# Revit family: Door-Exterior_Interior-Simpson-French-Full_Arch_Glass-Single
name_source: partatom
category: Doors
revit_build: Autodesk Revit Architecture 2012 (Build: 20110916_2132(x64)
units: mm (PartAtom-declared; Revit-internal decimal feet)

## types (273) — shared parameters
Arch Bottom Height = 0' - 7 19/32"
Assembly Code = B2030230
Bottom Rail Height = 0' - 8 13/16"
Construction Type = Wood
Frame = Wood - Simpson Doors - Douglas Fir
Frame Projection Ext. = 0' - 1"
Frame Projection Int. = 0' - 1"
Frame Type = Frame : Standard
Frame Width = 0' - 3"
Function = Exterior
Glass = Glass - Simpson Doors - Clear
Glass Options = http://simpsondoor.com
Manufacturer = Simpsons Door Company
Middle Rail Height = 0' - 6 3/4"
Muntin Width = 0' - 0 1/2"
Ovolo Construction = Yes
Panel = Wood - Simpson Doors - Douglas Fir
Panel Stile Width = 0' - 4 1/8"
Product Documentation Link = http://www.simpsondoor.com
Product Page URL = http://www.simpsondoor.com
Thickness = 0' - 1 3/4"
Thickness Note = comes in 1 3/4" and 2 1/4" Thickness. Default is set to 1 3/4"
Top Rail Height = 0' - 4 1/32"
URL = http://www.simpsondoor.com
UltraBlock Note = This Door Comes with The Option of UltraBlock Technology. It is Turn On as a Default
UltraBlock Option = Yes
Wall Closure = By host
WaterBarrier Note = This Door Comes with The Option of WaterBarrier with UltraBlock Technology. It is Turn Off as a Default
WaterBarrier with UltraBlock Technology = No
Wood Species = http://simpsondoor.com
Wood Species Note = Available in Any Wood Species

## per-type parameters (varying)
| type | Description | Height | Model | Number of Horizontal Muntins | Number of Vertical Muntins | Rough Height | Rough Width | Width |
| 1401 Exterior French 30x80 Ovolo Flat Panel | Exterior French - Single Lite | 6' - 8" | 1401 | 0 | 0 | 6' - 10" | 2' - 10" | 2' - 6" |
| 1401 Exterior French 30x84 Ovolo Flat Panel | Exterior French - Single Lite | 7' - 0" | 1401 | 0 | 0 | 7' - 2" | 2' - 10" | 2' - 6" |
| 1401 Exterior French 30x96 Ovolo Flat Panel | Exterior French - Single Lite | 8' - 0" | 1401 | 0 | 0 | 8' - 2" | 2' - 10" | 2' - 6" |
| 1401 Exterior French 32x80 Ovolo Flat Panel | Exterior French - Single Lite | 6' - 8" | 1401 | 0 | 0 | 6' - 10" | 3' - 0" | 2' - 8" |
| 1401 Exterior French 32x84 Ovolo Flat Panel | Exterior French - Single Lite | 7' - 0" | 1401 | 0 | 0 | 7' - 2" | 3' - 0" | 2' - 8" |
| 1401 Exterior French 32x96 Ovolo Flat Panel | Exterior French - Single Lite | 8' - 0" | 1401 | 0 | 0 | 8' - 2" | 3' - 0" | 2' - 8" |
| 1401 Exterior French 34x80 Ovolo Flat Panel | Exterior French - Single Lite | 6' - 8" | 1401 | 0 | 0 | 6' - 10" | 3' - 2" | 2' - 10" |
| 1401 Exterior French 34x84 Ovolo Flat Panel | Exterior French - Single Lite | 7' - 0" | 1401 | 0 | 0 | 7' - 2" | 3' - 2" | 2' - 10" |
| 1401 Exterior French 34x96 Ovolo Flat Panel | Exterior French - Single Lite | 8' - 0" | 1401 | 0 | 0 | 8' - 2" | 3' - 2" | 2' - 10" |
| 1401 Exterior French 36x80 Ovolo Flat Panel | Exterior French - Single Lite | 6' - 8" | 1401 | 0 | 0 | 6' - 10" | 3' - 4" | 3' - 0" |
| 1401 Exterior French 36x84 Ovolo Flat Panel | Exterior French - Single Lite | 7' - 0" | 1401 | 0 | 0 | 7' - 2" | 3' - 4" | 3' - 0" |
| 1401 Exterior French 36x96 Ovolo Flat Panel | Exterior French - Single Lite | 8' - 0" | 1401 | 0 | 0 | 8' - 2" | 3' - 4" | 3' - 0" |
| 1401 Exterior French 38x80 Ovolo Flat Panel | Exterior French - Single Lite | 6' - 8" | 1401 | 0 | 0 | 6' - 10" | 3' - 6" | 3' - 2" |
| 1401 Exterior French 38x84 Ovolo Flat Panel | Exterior French - Single Lite | 7' - 0" | 1401 | 0 | 0 | 7' - 2" | 3' - 6" | 3' - 2" |
| 1401 Exterior French 38x96 Ovolo Flat Panel | Exterior French - Single Lite | 8' - 0" | 1401 | 0 | 0 | 8' - 2" | 3' - 6" | 3' - 2" |
| 1401 Exterior French 40x80 Ovolo Flat Panel | Exterior French - Single Lite | 6' - 8" | 1401 | 0 | 0 | 6' - 10" | 3' - 8" | 3' - 4" |
| 1401 Exterior French 40x84 Ovolo Flat Panel | Exterior French - Single Lite | 7' - 0" | 1401 | 0 | 0 | 7' - 2" | 3' - 8" | 3' - 4" |
| 1401 Exterior French 40x96 Ovolo Flat Panel | Exterior French - Single Lite | 8' - 0" | 1401 | 0 | 0 | 8' - 2" | 3' - 8" | 3' - 4" |
| 1401 Exterior French 42x80 Ovolo Flat Panel | Exterior French - Single Lite | 6' - 8" | 1401 | 0 | 0 | 6' - 10" | 3' - 10" | 3' - 6" |
| 1401 Exterior French 42x84 Ovolo Flat Panel | Exterior French - Single Lite | 7' - 0" | 1401 | 0 | 0 | 7' - 2" | 3' - 10" | 3' - 6" |
| 1401 Exterior French 42x96 Ovolo Flat Panel | Exterior French - Single Lite | 8' - 0" | 1401 | 0 | 0 | 8' - 2" | 3' - 10" | 3' - 6" |
| 1410 Exterior French 30x80 Ovolo Flat Panel | Exterior French - Ten Lite | 6' - 8" | 1410 | 4 | 1 | 6' - 10" | 2' - 10" | 2' - 6" |
| 1410 Exterior French 30x84 Ovolo Flat Panel | Exterior French - Ten Lite | 7' - 0" | 1410 | 4 | 1 | 7' - 2" | 2' - 10" | 2' - 6" |
| 1410 Exterior French 30x96 Ovolo Flat Panel | Exterior French - Ten Lite | 8' - 0" | 1410 | 4 | 1 | 8' - 2" | 2' - 10" | 2' - 6" |
| 1410 Exterior French 32x80 Ovolo Flat Panel | Exterior French - Ten Lite | 6' - 8" | 1410 | 4 | 1 | 6' - 10" | 3' - 0" | 2' - 8" |
| 1410 Exterior French 32x84 Ovolo Flat Panel | Exterior French - Ten Lite | 7' - 0" | 1410 | 4 | 1 | 7' - 2" | 3' - 0" | 2' - 8" |
| 1410 Exterior French 32x96 Ovolo Flat Panel | Exterior French - Ten Lite | 8' - 0" | 1410 | 4 | 1 | 8' - 2" | 3' - 0" | 2' - 8" |
| 1410 Exterior French 34x80 Ovolo Flat Panel | Exterior French - Ten Lite | 6' - 8" | 1410 | 4 | 1 | 6' - 10" | 3' - 2" | 2' - 10" |
| 1410 Exterior French 34x84 Ovolo Flat Panel | Exterior French - Ten Lite | 7' - 0" | 1410 | 4 | 1 | 7' - 2" | 3' - 2" | 2' - 10" |
| 1410 Exterior French 34x96 Ovolo Flat Panel | Exterior French - Ten Lite | 8' - 0" | 1410 | 4 | 1 | 8' - 2" | 3' - 2" | 2' - 10" |
| 1410 Exterior French 36x80 Ovolo Flat Panel | Exterior French - Ten Lite | 6' - 8" | 1410 | 4 | 1 | 6' - 10" | 3' - 4" | 3' - 0" |
| 1410 Exterior French 36x84 Ovolo Flat Panel | Exterior French - Ten Lite | 7' - 0" | 1410 | 4 | 1 | 7' - 2" | 3' - 4" | 3' - 0" |
| 1410 Exterior French 36x96 Ovolo Flat Panel | Exterior French - Ten Lite | 8' - 0" | 1410 | 4 | 1 | 8' - 2" | 3' - 4" | 3' - 0" |
| 1410 Exterior French 38x80 Ovolo Flat Panel | Exterior French - Ten Lite | 6' - 8" | 1410 | 4 | 1 | 6' - 10" | 3' - 6" | 3' - 2" |
| 1410 Exterior French 38x84 Ovolo Flat Panel | Exterior French - Ten Lite | 7' - 0" | 1410 | 4 | 1 | 7' - 2" | 3' - 6" | 3' - 2" |
| 1410 Exterior French 38x96 Ovolo Flat Panel | Exterior French - Ten Lite | 8' - 0" | 1410 | 4 | 1 | 8' - 2" | 3' - 6" | 3' - 2" |
| 1410 Exterior French 40x80 Ovolo Flat Panel | Exterior French - Ten Lite | 6' - 8" | 1410 | 4 | 1 | 6' - 10" | 3' - 8" | 3' - 4" |
| 1410 Exterior French 40x84 Ovolo Flat Panel | Exterior French - Ten Lite | 7' - 0" | 1410 | 4 | 1 | 7' - 2" | 3' - 8" | 3' - 4" |
| 1410 Exterior French 40x96 Ovolo Flat Panel | Exterior French - Ten Lite | 8' - 0" | 1410 | 4 | 1 | 8' - 2" | 3' - 8" | 3' - 4" |
| 1410 Exterior French 42x80 Ovolo Flat Panel | Exterior French - Ten Lite | 6' - 8" | 1410 | 4 | 1 | 6' - 10" | 3' - 10" | 3' - 6" |
| 1410 Exterior French 42x84 Ovolo Flat Panel | Exterior French - Ten Lite | 7' - 0" | 1410 | 4 | 1 | 7' - 2" | 3' - 10" | 3' - 6" |
| 1410 Exterior French 42x96 Ovolo Flat Panel | Exterior French - Ten Lite | 8' - 0" | 1410 | 4 | 1 | 8' - 2" | 3' - 10" | 3' - 6" |
| 1415 Exterior French 30x80 Ovolo Flat Panel | Exterior French - Fifteen Lite | 6' - 8" | 1415 | 4 | 2 | 6' - 10" | 2' - 10" | 2' - 6" |
| 1415 Exterior French 30x84 Ovolo Flat Panel | Exterior French - Fifteen Lite | 7' - 0" | 1415 | 4 | 2 | 7' - 2" | 2' - 10" | 2' - 6" |
| 1415 Exterior French 30x96 Ovolo Flat Panel | Exterior French - Fifteen Lite | 8' - 0" | 1415 | 4 | 2 | 8' - 2" | 2' - 10" | 2' - 6" |
| 1415 Exterior French 32x80 Ovolo Flat Panel | Exterior French - Fifteen Lite | 6' - 8" | 1415 | 4 | 2 | 6' - 10" | 3' - 0" | 2' - 8" |
| 1415 Exterior French 32x84 Ovolo Flat Panel | Exterior French - Fifteen Lite | 7' - 0" | 1415 | 4 | 2 | 7' - 2" | 3' - 0" | 2' - 8" |
| 1415 Exterior French 32x96 Ovolo Flat Panel | Exterior French - Fifteen Lite | 8' - 0" | 1415 | 4 | 2 | 8' - 2" | 3' - 0" | 2' - 8" |
| 1415 Exterior French 34x80 Ovolo Flat Panel | Exterior French - Fifteen Lite | 6' - 8" | 1415 | 4 | 2 | 6' - 10" | 3' - 2" | 2' - 10" |
| 1415 Exterior French 34x84 Ovolo Flat Panel | Exterior French - Fifteen Lite | 7' - 0" | 1415 | 4 | 2 | 7' - 2" | 3' - 2" | 2' - 10" |
| 1415 Exterior French 34x96 Ovolo Flat Panel | Exterior French - Fifteen Lite | 8' - 0" | 1415 | 4 | 2 | 8' - 2" | 3' - 2" | 2' - 10" |
| 1415 Exterior French 36x80 Ovolo Flat Panel | Exterior French - Fifteen Lite | 6' - 8" | 1415 | 4 | 2 | 6' - 10" | 3' - 4" | 3' - 0" |
| 1415 Exterior French 36x84 Ovolo Flat Panel | Exterior French - Fifteen Lite | 7' - 0" | 1415 | 4 | 2 | 7' - 2" | 3' - 4" | 3' - 0" |
| 1415 Exterior French 36x96 Ovolo Flat Panel | Exterior French - Fifteen Lite | 8' - 0" | 1415 | 4 | 2 | 8' - 2" | 3' - 4" | 3' - 0" |
| 1415 Exterior French 38x80 Ovolo Flat Panel | Exterior French - Fifteen Lite | 6' - 8" | 1415 | 4 | 2 | 6' - 10" | 3' - 6" | 3' - 2" |
| 1415 Exterior French 38x84 Ovolo Flat Panel | Exterior French - Fifteen Lite | 7' - 0" | 1415 | 4 | 2 | 7' - 2" | 3' - 6" | 3' - 2" |
| 1415 Exterior French 38x96 Ovolo Flat Panel | Exterior French - Fifteen Lite | 8' - 0" | 1415 | 4 | 2 | 8' - 2" | 3' - 6" | 3' - 2" |
| 1415 Exterior French 40x80 Ovolo Flat Panel | Exterior French - Fifteen Lite | 6' - 8" | 1415 | 4 | 2 | 6' - 10" | 3' - 8" | 3' - 4" |
| 1415 Exterior French 40x84 Ovolo Flat Panel | Exterior French - Fifteen Lite | 7' - 0" | 1415 | 4 | 2 | 7' - 2" | 3' - 8" | 3' - 4" |
| 1415 Exterior French 40x96 Ovolo Flat Panel | Exterior French - Fifteen Lite | 8' - 0" | 1415 | 4 | 2 | 8' - 2" | 3' - 8" | 3' - 4" |
| 1415 Exterior French 42x80 Ovolo Flat Panel | Exterior French - Fifteen Lite | 6' - 8" | 1415 | 4 | 2 | 6' - 10" | 3' - 10" | 3' - 6" |
| 1415 Exterior French 42x84 Ovolo Flat Panel | Exterior French - Fifteen Lite | 7' - 0" | 1415 | 4 | 2 | 7' - 2" | 3' - 10" | 3' - 6" |
| 1415 Exterior French 42x96 Ovolo Flat Panel | Exterior French - Fifteen Lite | 8' - 0" | 1415 | 4 | 2 | 8' - 2" | 3' - 10" | 3' - 6" |
| 1416 Exterior French 30x80 Ovolo Flat Panel | Exterior French - Six Lite | 6' - 8" | 1416 | 2 | 1 | 6' - 10" | 2' - 10" | 2' - 6" |
| 1416 Exterior French 30x84 Ovolo Flat Panel | Exterior French - Six Lite | 7' - 0" | 1416 | 2 | 1 | 7' - 2" | 2' - 10" | 2' - 6" |
| 1416 Exterior French 30x96 Ovolo Flat Panel | Exterior French - Six Lite | 8' - 0" | 1416 | 2 | 1 | 8' - 2" | 2' - 10" | 2' - 6" |
| 1416 Exterior French 32x80 Ovolo Flat Panel | Exterior French - Six Lite | 6' - 8" | 1416 | 2 | 1 | 6' - 10" | 3' - 0" | 2' - 8" |
| 1416 Exterior French 32x84 Ovolo Flat Panel | Exterior French - Six Lite | 7' - 0" | 1416 | 2 | 1 | 7' - 2" | 3' - 0" | 2' - 8" |
| 1416 Exterior French 32x96 Ovolo Flat Panel | Exterior French - Six Lite | 8' - 0" | 1416 | 2 | 1 | 8' - 2" | 3' - 0" | 2' - 8" |
| 1416 Exterior French 34x80 Ovolo Flat Panel | Exterior French - Six Lite | 6' - 8" | 1416 | 2 | 1 | 6' - 10" | 3' - 2" | 2' - 10" |
| 1416 Exterior French 34x84 Ovolo Flat Panel | Exterior French - Six Lite | 7' - 0" | 1416 | 2 | 1 | 7' - 2" | 3' - 2" | 2' - 10" |
| 1416 Exterior French 34x96 Ovolo Flat Panel | Exterior French - Six Lite | 8' - 0" | 1416 | 2 | 1 | 8' - 2" | 3' - 2" | 2' - 10" |
| 1416 Exterior French 36x80 Ovolo Flat Panel | Exterior French - Six Lite | 6' - 8" | 1416 | 2 | 1 | 6' - 10" | 3' - 4" | 3' - 0" |
| 1416 Exterior French 36x84 Ovolo Flat Panel | Exterior French - Six Lite | 7' - 0" | 1416 | 2 | 1 | 7' - 2" | 3' - 4" | 3' - 0" |
| 1416 Exterior French 36x96 Ovolo Flat Panel | Exterior French - Six Lite | 8' - 0" | 1416 | 2 | 1 | 8' - 2" | 3' - 4" | 3' - 0" |
| 1416 Exterior French 38x80 Ovolo Flat Panel | Exterior French - Six Lite | 6' - 8" | 1416 | 2 | 1 | 6' - 10" | 3' - 6" | 3' - 2" |
| 1416 Exterior French 38x84 Ovolo Flat Panel | Exterior French - Six Lite | 7' - 0" | 1416 | 2 | 1 | 7' - 2" | 3' - 6" | 3' - 2" |
| 1416 Exterior French 38x96 Ovolo Flat Panel | Exterior French - Six Lite | 8' - 0" | 1416 | 2 | 1 | 8' - 2" | 3' - 6" | 3' - 2" |
| 1416 Exterior French 40x80 Ovolo Flat Panel | Exterior French - Six Lite | 6' - 8" | 1416 | 2 | 1 | 6' - 10" | 3' - 8" | 3' - 4" |
| 1416 Exterior French 40x84 Ovolo Flat Panel | Exterior French - Six Lite | 7' - 0" | 1416 | 2 | 1 | 7' - 2" | 3' - 8" | 3' - 4" |
| 1416 Exterior French 40x96 Ovolo Flat Panel | Exterior French - Six Lite | 8' - 0" | 1416 | 2 | 1 | 8' - 2" | 3' - 8" | 3' - 4" |
| 1416 Exterior French 42x80 Ovolo Flat Panel | Exterior French - Six Lite | 6' - 8" | 1416 | 2 | 1 | 6' - 10" | 3' - 10" | 3' - 6" |
| 1416 Exterior French 42x84 Ovolo Flat Panel | Exterior French - Six Lite | 7' - 0" | 1416 | 2 | 1 | 7' - 2" | 3' - 10" | 3' - 6" |
| 1416 Exterior French 42x96 Ovolo Flat Panel | Exterior French - Six Lite | 8' - 0" | 1416 | 2 | 1 | 8' - 2" | 3' - 10" | 3' - 6" |
| 1418 Exterior French 30x80 Ovolo Flat Panel | Exterior French - Eight Lite | 6' - 8" | 1418 | 3 | 1 | 6' - 10" | 2' - 10" | 2' - 6" |
| 1418 Exterior French 30x84 Ovolo Flat Panel | Exterior French - Eight Lite | 7' - 0" | 1418 | 3 | 1 | 7' - 2" | 2' - 10" | 2' - 6" |
| 1418 Exterior French 30x96 Ovolo Flat Panel | Exterior French - Eight Lite | 8' - 0" | 1418 | 3 | 1 | 8' - 2" | 2' - 10" | 2' - 6" |
| 1418 Exterior French 32x80 Ovolo Flat Panel | Exterior French - Eight Lite | 6' - 8" | 1418 | 3 | 1 | 6' - 10" | 3' - 0" | 2' - 8" |
| 1418 Exterior French 32x84 Ovolo Flat Panel | Exterior French - Eight Lite | 7' - 0" | 1418 | 3 | 1 | 7' - 2" | 3' - 0" | 2' - 8" |
| 1418 Exterior French 32x96 Ovolo Flat Panel | Exterior French - Eight Lite | 8' - 0" | 1418 | 3 | 1 | 8' - 2" | 3' - 0" | 2' - 8" |
| 1418 Exterior French 34x80 Ovolo Flat Panel | Exterior French - Eight Lite | 6' - 8" | 1418 | 3 | 1 | 6' - 10" | 3' - 2" | 2' - 10" |
| 1418 Exterior French 34x84 Ovolo Flat Panel | Exterior French - Eight Lite | 7' - 0" | 1418 | 3 | 1 | 7' - 2" | 3' - 2" | 2' - 10" |
| 1418 Exterior French 34x96 Ovolo Flat Panel | Exterior French - Eight Lite | 8' - 0" | 1418 | 3 | 1 | 8' - 2" | 3' - 2" | 2' - 10" |
| 1418 Exterior French 36x80 Ovolo Flat Panel | Exterior French - Eight Lite | 6' - 8" | 1418 | 3 | 1 | 6' - 10" | 3' - 4" | 3' - 0" |
| 1418 Exterior French 36x84 Ovolo Flat Panel | Exterior French - Eight Lite | 7' - 0" | 1418 | 3 | 1 | 7' - 2" | 3' - 4" | 3' - 0" |
| 1418 Exterior French 36x96 Ovolo Flat Panel | Exterior French - Eight Lite | 8' - 0" | 1418 | 3 | 1 | 8' - 2" | 3' - 4" | 3' - 0" |
| 1418 Exterior French 38x80 Ovolo Flat Panel | Exterior French - Eight Lite | 6' - 8" | 1418 | 3 | 1 | 6' - 10" | 3' - 6" | 3' - 2" |
| 1418 Exterior French 38x84 Ovolo Flat Panel | Exterior French - Eight Lite | 7' - 0" | 1418 | 3 | 1 | 7' - 2" | 3' - 6" | 3' - 2" |
| 1418 Exterior French 38x96 Ovolo Flat Panel | Exterior French - Eight Lite | 8' - 0" | 1418 | 3 | 1 | 8' - 2" | 3' - 6" | 3' - 2" |
| 1418 Exterior French 40x80 Ovolo Flat Panel | Exterior French - Eight Lite | 6' - 8" | 1418 | 3 | 1 | 6' - 10" | 3' - 8" | 3' - 4" |
| 1418 Exterior French 40x84 Ovolo Flat Panel | Exterior French - Eight Lite | 7' - 0" | 1418 | 3 | 1 | 7' - 2" | 3' - 8" | 3' - 4" |
| 1418 Exterior French 40x96 Ovolo Flat Panel | Exterior French - Eight Lite | 8' - 0" | 1418 | 3 | 1 | 8' - 2" | 3' - 8" | 3' - 4" |
| 1418 Exterior French 42x80 Ovolo Flat Panel | Exterior French - Eight Lite | 6' - 8" | 1418 | 3 | 1 | 6' - 10" | 3' - 10" | 3' - 6" |
| 1418 Exterior French 42x84 Ovolo Flat Panel | Exterior French - Eight Lite | 7' - 0" | 1418 | 3 | 1 | 7' - 2" | 3' - 10" | 3' - 6" |
| 1418 Exterior French 42x96 Ovolo Flat Panel | Exterior French - Eight Lite | 8' - 0" | 1418 | 3 | 1 | 8' - 2" | 3' - 10" | 3' - 6" |
| 7051 Thermal French 30x80 Ovolo Flat Panel | Thermal French TDL - Single Lite | 6' - 8" | 7051 | 0 | 0 | 6' - 10" | 2' - 10" | 2' - 6" |
| 7051 Thermal French 30x84 Ovolo Flat Panel | Thermal French TDL - Single Lite | 7' - 0" | 7051 | 0 | 0 | 7' - 2" | 2' - 10" | 2' - 6" |
| 7051 Thermal French 30x96 Ovolo Flat Panel | Thermal French TDL - Single Lite | 8' - 0" | 7051 | 0 | 0 | 8' - 2" | 2' - 10" | 2' - 6" |
| 7051 Thermal French 32x80 Ovolo Flat Panel | Thermal French TDL - Single Lite | 6' - 8" | 7051 | 0 | 0 | 6' - 10" | 3' - 0" | 2' - 8" |
| 7051 Thermal French 32x84 Ovolo Flat Panel | Thermal French TDL - Single Lite | 7' - 0" | 7051 | 0 | 0 | 7' - 2" | 3' - 0" | 2' - 8" |
| 7051 Thermal French 32x96 Ovolo Flat Panel | Thermal French TDL - Single Lite | 8' - 0" | 7051 | 0 | 0 | 8' - 2" | 3' - 0" | 2' - 8" |
| 7051 Thermal French 34x80 Ovolo Flat Panel | Thermal French TDL - Single Lite | 6' - 8" | 7051 | 0 | 0 | 6' - 10" | 3' - 2" | 2' - 10" |
| 7051 Thermal French 34x84 Ovolo Flat Panel | Thermal French TDL - Single Lite | 7' - 0" | 7051 | 0 | 0 | 7' - 2" | 3' - 2" | 2' - 10" |
| 7051 Thermal French 34x96 Ovolo Flat Panel | Thermal French TDL - Single Lite | 8' - 0" | 7051 | 0 | 0 | 8' - 2" | 3' - 2" | 2' - 10" |
| 7051 Thermal French 36x80 Ovolo Flat Panel | Thermal French TDL - Single Lite | 6' - 8" | 7051 | 0 | 0 | 6' - 10" | 3' - 4" | 3' - 0" |
| 7051 Thermal French 36x84 Ovolo Flat Panel | Thermal French TDL - Single Lite | 7' - 0" | 7051 | 0 | 0 | 7' - 2" | 3' - 4" | 3' - 0" |
| 7051 Thermal French 36x96 Ovolo Flat Panel | Thermal French TDL - Single Lite | 8' - 0" | 7051 | 0 | 0 | 8' - 2" | 3' - 4" | 3' - 0" |
| 7051 Thermal French 38x80 Ovolo Flat Panel | Thermal French TDL - Single Lite | 6' - 8" | 7051 | 0 | 0 | 6' - 10" | 3' - 6" | 3' - 2" |
| 7051 Thermal French 38x84 Ovolo Flat Panel | Thermal French TDL - Single Lite | 7' - 0" | 7051 | 0 | 0 | 7' - 2" | 3' - 6" | 3' - 2" |
| 7051 Thermal French 38x96 Ovolo Flat Panel | Thermal French TDL - Single Lite | 8' - 0" | 7051 | 0 | 0 | 8' - 2" | 3' - 6" | 3' - 2" |
| 7051 Thermal French 40x80 Ovolo Flat Panel | Thermal French TDL - Single Lite | 6' - 8" | 7051 | 0 | 0 | 6' - 10" | 3' - 8" | 3' - 4" |
| 7051 Thermal French 40x84 Ovolo Flat Panel | Thermal French TDL - Single Lite | 7' - 0" | 7051 | 0 | 0 | 7' - 2" | 3' - 8" | 3' - 4" |
| 7051 Thermal French 40x96 Ovolo Flat Panel | Thermal French TDL - Single Lite | 8' - 0" | 7051 | 0 | 0 | 8' - 2" | 3' - 8" | 3' - 4" |
| 7051 Thermal French 42x80 Ovolo Flat Panel | Thermal French TDL - Single Lite | 6' - 8" | 7051 | 0 | 0 | 6' - 10" | 3' - 10" | 3' - 6" |
| 7051 Thermal French 42x84 Ovolo Flat Panel | Thermal French TDL - Single Lite | 7' - 0" | 7051 | 0 | 0 | 7' - 2" | 3' - 10" | 3' - 6" |
| 7051 Thermal French 42x96 Ovolo Flat Panel | Thermal French TDL - Single Lite | 8' - 0" | 7051 | 0 | 0 | 8' - 2" | 3' - 10" | 3' - 6" |
| 7055 Thermal French 30x80 Ovolo Flat Panel | Thermal French TDL - Fifteen Lite | 6' - 8" | 7055 | 4 | 2 | 6' - 10" | 2' - 10" | 2' - 6" |
| 7055 Thermal French 30x84 Ovolo Flat Panel | Thermal French TDL - Fifteen Lite | 7' - 0" | 7055 | 4 | 2 | 7' - 2" | 2' - 10" | 2' - 6" |
| 7055 Thermal French 30x96 Ovolo Flat Panel | Thermal French TDL - Fifteen Lite | 8' - 0" | 7055 | 4 | 2 | 8' - 2" | 2' - 10" | 2' - 6" |
| 7055 Thermal French 32x80 Ovolo Flat Panel | Thermal French TDL - Fifteen Lite | 6' - 8" | 7055 | 4 | 2 | 6' - 10" | 3' - 0" | 2' - 8" |
| 7055 Thermal French 32x84 Ovolo Flat Panel | Thermal French TDL - Fifteen Lite | 7' - 0" | 7055 | 4 | 2 | 7' - 2" | 3' - 0" | 2' - 8" |
| 7055 Thermal French 32x96 Ovolo Flat Panel | Thermal French TDL - Fifteen Lite | 8' - 0" | 7055 | 4 | 2 | 8' - 2" | 3' - 0" | 2' - 8" |
| 7055 Thermal French 34x80 Ovolo Flat Panel | Thermal French TDL - Fifteen Lite | 6' - 8" | 7055 | 4 | 2 | 6' - 10" | 3' - 2" | 2' - 10" |
| 7055 Thermal French 34x84 Ovolo Flat Panel | Thermal French TDL - Fifteen Lite | 7' - 0" | 7055 | 4 | 2 | 7' - 2" | 3' - 2" | 2' - 10" |
| 7055 Thermal French 34x96 Ovolo Flat Panel | Thermal French TDL - Fifteen Lite | 8' - 0" | 7055 | 4 | 2 | 8' - 2" | 3' - 2" | 2' - 10" |
| 7055 Thermal French 36x80 Ovolo Flat Panel | Thermal French TDL - Fifteen Lite | 6' - 8" | 7055 | 4 | 2 | 6' - 10" | 3' - 4" | 3' - 0" |
| 7055 Thermal French 36x84 Ovolo Flat Panel | Thermal French TDL - Fifteen Lite | 7' - 0" | 7055 | 4 | 2 | 7' - 2" | 3' - 4" | 3' - 0" |
| 7055 Thermal French 36x96 Ovolo Flat Panel | Thermal French TDL - Fifteen Lite | 8' - 0" | 7055 | 4 | 2 | 8' - 2" | 3' - 4" | 3' - 0" |
| 7055 Thermal French 38x80 Ovolo Flat Panel | Thermal French TDL - Fifteen Lite | 6' - 8" | 7055 | 4 | 2 | 6' - 10" | 3' - 6" | 3' - 2" |
| 7055 Thermal French 38x84 Ovolo Flat Panel | Thermal French TDL - Fifteen Lite | 7' - 0" | 7055 | 4 | 2 | 7' - 2" | 3' - 6" | 3' - 2" |
| 7055 Thermal French 38x96 Ovolo Flat Panel | Thermal French TDL - Fifteen Lite | 8' - 0" | 7055 | 4 | 2 | 8' - 2" | 3' - 6" | 3' - 2" |
| 7055 Thermal French 40x80 Ovolo Flat Panel | Thermal French TDL - Fifteen Lite | 6' - 8" | 7055 | 4 | 2 | 6' - 10" | 3' - 8" | 3' - 4" |
| 7055 Thermal French 40x84 Ovolo Flat Panel | Thermal French TDL - Fifteen Lite | 7' - 0" | 7055 | 4 | 2 | 7' - 2" | 3' - 8" | 3' - 4" |
| 7055 Thermal French 40x96 Ovolo Flat Panel | Thermal French TDL - Fifteen Lite | 8' - 0" | 7055 | 4 | 2 | 8' - 2" | 3' - 8" | 3' - 4" |
| 7055 Thermal French 42x80 Ovolo Flat Panel | Thermal French TDL - Fifteen Lite | 6' - 8" | 7055 | 4 | 2 | 6' - 10" | 3' - 10" | 3' - 6" |
| 7055 Thermal French 42x84 Ovolo Flat Panel | Thermal French TDL - Fifteen Lite | 7' - 0" | 7055 | 4 | 2 | 7' - 2" | 3' - 10" | 3' - 6" |
| 7055 Thermal French 42x96 Ovolo Flat Panel | Thermal French TDL - Fifteen Lite | 8' - 0" | 7055 | 4 | 2 | 8' - 2" | 3' - 10" | 3' - 6" |
| 7056 Thermal French 30x80 Ovolo Flat Panel | Thermal French TDL - Six Lite | 6' - 8" | 7056 | 2 | 1 | 6' - 10" | 2' - 10" | 2' - 6" |
| 7056 Thermal French 30x84 Ovolo Flat Panel | Thermal French TDL - Six Lite | 7' - 0" | 7056 | 2 | 1 | 7' - 2" | 2' - 10" | 2' - 6" |
| 7056 Thermal French 30x96 Ovolo Flat Panel | Thermal French TDL - Six Lite | 8' - 0" | 7056 | 2 | 1 | 8' - 2" | 2' - 10" | 2' - 6" |
| 7056 Thermal French 32x80 Ovolo Flat Panel | Thermal French TDL - Six Lite | 6' - 8" | 7056 | 2 | 1 | 6' - 10" | 3' - 0" | 2' - 8" |
| 7056 Thermal French 32x84 Ovolo Flat Panel | Thermal French TDL - Six Lite | 7' - 0" | 7056 | 2 | 1 | 7' - 2" | 3' - 0" | 2' - 8" |
| 7056 Thermal French 32x96 Ovolo Flat Panel | Thermal French TDL - Six Lite | 8' - 0" | 7056 | 2 | 1 | 8' - 2" | 3' - 0" | 2' - 8" |
| 7056 Thermal French 34x80 Ovolo Flat Panel | Thermal French TDL - Six Lite | 6' - 8" | 7056 | 2 | 1 | 6' - 10" | 3' - 2" | 2' - 10" |
| 7056 Thermal French 34x84 Ovolo Flat Panel | Thermal French TDL - Six Lite | 7' - 0" | 7056 | 2 | 1 | 7' - 2" | 3' - 2" | 2' - 10" |
| 7056 Thermal French 34x96 Ovolo Flat Panel | Thermal French TDL - Six Lite | 8' - 0" | 7056 | 2 | 1 | 8' - 2" | 3' - 2" | 2' - 10" |
| 7056 Thermal French 36x80 Ovolo Flat Panel | Thermal French TDL - Six Lite | 6' - 8" | 7056 | 2 | 1 | 6' - 10" | 3' - 4" | 3' - 0" |
| 7056 Thermal French 36x84 Ovolo Flat Panel | Thermal French TDL - Six Lite | 7' - 0" | 7056 | 2 | 1 | 7' - 2" | 3' - 4" | 3' - 0" |
| 7056 Thermal French 36x96 Ovolo Flat Panel | Thermal French TDL - Six Lite | 8' - 0" | 7056 | 2 | 1 | 8' - 2" | 3' - 4" | 3' - 0" |
| 7056 Thermal French 38x80 Ovolo Flat Panel | Thermal French TDL - Six Lite | 6' - 8" | 7056 | 2 | 1 | 6' - 10" | 3' - 6" | 3' - 2" |
| 7056 Thermal French 38x84 Ovolo Flat Panel | Thermal French TDL - Six Lite | 7' - 0" | 7056 | 2 | 1 | 7' - 2" | 3' - 6" | 3' - 2" |
| 7056 Thermal French 38x96 Ovolo Flat Panel | Thermal French TDL - Six Lite | 8' - 0" | 7056 | 2 | 1 | 8' - 2" | 3' - 6" | 3' - 2" |
| 7056 Thermal French 40x80 Ovolo Flat Panel | Thermal French TDL - Six Lite | 6' - 8" | 7056 | 2 | 1 | 6' - 10" | 3' - 8" | 3' - 4" |
| 7056 Thermal French 40x84 Ovolo Flat Panel | Thermal French TDL - Six Lite | 7' - 0" | 7056 | 2 | 1 | 7' - 2" | 3' - 8" | 3' - 4" |
| 7056 Thermal French 40x96 Ovolo Flat Panel | Thermal French TDL - Six Lite | 8' - 0" | 7056 | 2 | 1 | 8' - 2" | 3' - 8" | 3' - 4" |
| 7056 Thermal French 42x80 Ovolo Flat Panel | Thermal French TDL - Six Lite | 6' - 8" | 7056 | 2 | 1 | 6' - 10" | 3' - 10" | 3' - 6" |
| 7056 Thermal French 42x84 Ovolo Flat Panel | Thermal French TDL - Six Lite | 7' - 0" | 7056 | 2 | 1 | 7' - 2" | 3' - 10" | 3' - 6" |
| 7056 Thermal French 42x96 Ovolo Flat Panel | Thermal French TDL - Six Lite | 8' - 0" | 7056 | 2 | 1 | 8' - 2" | 3' - 10" | 3' - 6" |
| 7058 Thermal French 30x80 Ovolo Flat Panel | Thermal French TDL - Eight Lite | 6' - 8" | 7058 | 3 | 1 | 6' - 10" | 2' - 10" | 2' - 6" |
| 7058 Thermal French 30x84 Ovolo Flat Panel | Thermal French TDL - Eight Lite | 7' - 0" | 7058 | 3 | 1 | 7' - 2" | 2' - 10" | 2' - 6" |
| 7058 Thermal French 30x96 Ovolo Flat Panel | Thermal French TDL - Eight Lite | 8' - 0" | 7058 | 3 | 1 | 8' - 2" | 2' - 10" | 2' - 6" |
| 7058 Thermal French 32x80 Ovolo Flat Panel | Thermal French TDL - Eight Lite | 6' - 8" | 7058 | 3 | 1 | 6' - 10" | 3' - 0" | 2' - 8" |
| 7058 Thermal French 32x84 Ovolo Flat Panel | Thermal French TDL - Eight Lite | 7' - 0" | 7058 | 3 | 1 | 7' - 2" | 3' - 0" | 2' - 8" |
| 7058 Thermal French 32x96 Ovolo Flat Panel | Thermal French TDL - Eight Lite | 8' - 0" | 7058 | 3 | 1 | 8' - 2" | 3' - 0" | 2' - 8" |
| 7058 Thermal French 34x80 Ovolo Flat Panel | Thermal French TDL - Eight Lite | 6' - 8" | 7058 | 3 | 1 | 6' - 10" | 3' - 2" | 2' - 10" |
| 7058 Thermal French 34x84 Ovolo Flat Panel | Thermal French TDL - Eight Lite | 7' - 0" | 7058 | 3 | 1 | 7' - 2" | 3' - 2" | 2' - 10" |
| 7058 Thermal French 34x96 Ovolo Flat Panel | Thermal French TDL - Eight Lite | 8' - 0" | 7058 | 3 | 1 | 8' - 2" | 3' - 2" | 2' - 10" |
| 7058 Thermal French 36x80 Ovolo Flat Panel | Thermal French TDL - Eight Lite | 6' - 8" | 7058 | 3 | 1 | 6' - 10" | 3' - 4" | 3' - 0" |
| 7058 Thermal French 36x84 Ovolo Flat Panel | Thermal French TDL - Eight Lite | 7' - 0" | 7058 | 3 | 1 | 7' - 2" | 3' - 4" | 3' - 0" |
| 7058 Thermal French 36x96 Ovolo Flat Panel | Thermal French TDL - Eight Lite | 8' - 0" | 7058 | 3 | 1 | 8' - 2" | 3' - 4" | 3' - 0" |
| 7058 Thermal French 38x80 Ovolo Flat Panel | Thermal French TDL - Eight Lite | 6' - 8" | 7058 | 3 | 1 | 6' - 10" | 3' - 6" | 3' - 2" |
| 7058 Thermal French 38x84 Ovolo Flat Panel | Thermal French TDL - Eight Lite | 7' - 0" | 7058 | 3 | 1 | 7' - 2" | 3' - 6" | 3' - 2" |
| 7058 Thermal French 38x96 Ovolo Flat Panel | Thermal French TDL - Eight Lite | 8' - 0" | 7058 | 3 | 1 | 8' - 2" | 3' - 6" | 3' - 2" |
| 7058 Thermal French 40x80 Ovolo Flat Panel | Thermal French TDL - Eight Lite | 6' - 8" | 7058 | 3 | 1 | 6' - 10" | 3' - 8" | 3' - 4" |
| 7058 Thermal French 40x84 Ovolo Flat Panel | Thermal French TDL - Eight Lite | 7' - 0" | 7058 | 3 | 1 | 7' - 2" | 3' - 8" | 3' - 4" |
| 7058 Thermal French 40x96 Ovolo Flat Panel | Thermal French TDL - Eight Lite | 8' - 0" | 7058 | 3 | 1 | 8' - 2" | 3' - 8" | 3' - 4" |
| 7058 Thermal French 42x80 Ovolo Flat Panel | Thermal French TDL - Eight Lite | 6' - 8" | 7058 | 3 | 1 | 6' - 10" | 3' - 10" | 3' - 6" |
| 7058 Thermal French 42x84 Ovolo Flat Panel | Thermal French TDL - Eight Lite | 7' - 0" | 7058 | 3 | 1 | 7' - 2" | 3' - 10" | 3' - 6" |
| 7058 Thermal French 42x96 Ovolo Flat Panel | Thermal French TDL - Eight Lite | 8' - 0" | 7058 | 3 | 1 | 8' - 2" | 3' - 10" | 3' - 6" |
| 37050 Thermal French 30x80 Ovolo Flat Panel | Thermal French SDL - Ten Lite | 6' - 8" | 37050 | 4 | 1 | 6' - 10" | 2' - 10" | 2' - 6" |
| 37050 Thermal French 30x84 Ovolo Flat Panel | Thermal French SDL - Ten Lite | 7' - 0" | 37050 | 4 | 1 | 7' - 2" | 2' - 10" | 2' - 6" |
| 37050 Thermal French 30x96 Ovolo Flat Panel | Thermal French SDL - Ten Lite | 8' - 0" | 37050 | 4 | 1 | 8' - 2" | 2' - 10" | 2' - 6" |
| 37050 Thermal French 32x80 Ovolo Flat Panel | Thermal French SDL - Ten Lite | 6' - 8" | 37050 | 4 | 1 | 6' - 10" | 3' - 0" | 2' - 8" |
| 37050 Thermal French 32x84 Ovolo Flat Panel | Thermal French SDL - Ten Lite | 7' - 0" | 37050 | 4 | 1 | 7' - 2" | 3' - 0" | 2' - 8" |
| 37050 Thermal French 32x96 Ovolo Flat Panel | Thermal French SDL - Ten Lite | 8' - 0" | 37050 | 4 | 1 | 8' - 2" | 3' - 0" | 2' - 8" |
| 37050 Thermal French 34x80 Ovolo Flat Panel | Thermal French SDL - Ten Lite | 6' - 8" | 37050 | 4 | 1 | 6' - 10" | 3' - 2" | 2' - 10" |
| 37050 Thermal French 34x84 Ovolo Flat Panel | Thermal French SDL - Ten Lite | 7' - 0" | 37050 | 4 | 1 | 7' - 2" | 3' - 2" | 2' - 10" |
| 37050 Thermal French 34x96 Ovolo Flat Panel | Thermal French SDL - Ten Lite | 8' - 0" | 37050 | 4 | 1 | 8' - 2" | 3' - 2" | 2' - 10" |
| 37050 Thermal French 36x80 Ovolo Flat Panel | Thermal French SDL - Ten Lite | 6' - 8" | 37050 | 4 | 1 | 6' - 10" | 3' - 4" | 3' - 0" |
| 37050 Thermal French 36x84 Ovolo Flat Panel | Thermal French SDL - Ten Lite | 7' - 0" | 37050 | 4 | 1 | 7' - 2" | 3' - 4" | 3' - 0" |
| 37050 Thermal French 36x96 Ovolo Flat Panel | Thermal French SDL - Ten Lite | 8' - 0" | 37050 | 4 | 1 | 8' - 2" | 3' - 4" | 3' - 0" |
| 37050 Thermal French 38x80 Ovolo Flat Panel | Thermal French SDL - Ten Lite | 6' - 8" | 37050 | 4 | 1 | 6' - 10" | 3' - 6" | 3' - 2" |
| 37050 Thermal French 38x84 Ovolo Flat Panel | Thermal French SDL - Ten Lite | 7' - 0" | 37050 | 4 | 1 | 7' - 2" | 3' - 6" | 3' - 2" |
| 37050 Thermal French 38x96 Ovolo Flat Panel | Thermal French SDL - Ten Lite | 8' - 0" | 37050 | 4 | 1 | 8' - 2" | 3' - 6" | 3' - 2" |
| 37050 Thermal French 40x80 Ovolo Flat Panel | Thermal French SDL - Ten Lite | 6' - 8" | 37050 | 4 | 1 | 6' - 10" | 3' - 8" | 3' - 4" |
| 37050 Thermal French 40x84 Ovolo Flat Panel | Thermal French SDL - Ten Lite | 7' - 0" | 37050 | 4 | 1 | 7' - 2" | 3' - 8" | 3' - 4" |
| 37050 Thermal French 40x96 Ovolo Flat Panel | Thermal French SDL - Ten Lite | 8' - 0" | 37050 | 4 | 1 | 8' - 2" | 3' - 8" | 3' - 4" |
| 37050 Thermal French 42x80 Ovolo Flat Panel | Thermal French SDL - Ten Lite | 6' - 8" | 37050 | 4 | 1 | 6' - 10" | 3' - 10" | 3' - 6" |
| 37050 Thermal French 42x84 Ovolo Flat Panel | Thermal French SDL - Ten Lite | 7' - 0" | 37050 | 4 | 1 | 7' - 2" | 3' - 10" | 3' - 6" |
| 37050 Thermal French 42x96 Ovolo Flat Panel | Thermal French SDL - Ten Lite | 8' - 0" | 37050 | 4 | 1 | 8' - 2" | 3' - 10" | 3' - 6" |
| 37055 Thermal French 30x80 Ovolo Flat Panel | Thermal French TDL - Fifteen Lite | 6' - 8" | 37055 | 4 | 2 | 6' - 10" | 2' - 10" | 2' - 6" |
| 37055 Thermal French 30x84 Ovolo Flat Panel | Thermal French TDL - Fifteen Lite | 7' - 0" | 37055 | 4 | 2 | 7' - 2" | 2' - 10" | 2' - 6" |
| 37055 Thermal French 30x96 Ovolo Flat Panel | Thermal French TDL - Fifteen Lite | 8' - 0" | 37055 | 4 | 2 | 8' - 2" | 2' - 10" | 2' - 6" |
| 37055 Thermal French 32x80 Ovolo Flat Panel | Thermal French TDL - Fifteen Lite | 6' - 8" | 37055 | 4 | 2 | 6' - 10" | 3' - 0" | 2' - 8" |
| 37055 Thermal French 32x84 Ovolo Flat Panel | Thermal French TDL - Fifteen Lite | 7' - 0" | 37055 | 4 | 2 | 7' - 2" | 3' - 0" | 2' - 8" |
| 37055 Thermal French 32x96 Ovolo Flat Panel | Thermal French TDL - Fifteen Lite | 8' - 0" | 37055 | 4 | 2 | 8' - 2" | 3' - 0" | 2' - 8" |
| 37055 Thermal French 34x80 Ovolo Flat Panel | Thermal French TDL - Fifteen Lite | 6' - 8" | 37055 | 4 | 2 | 6' - 10" | 3' - 2" | 2' - 10" |
| 37055 Thermal French 34x84 Ovolo Flat Panel | Thermal French TDL - Fifteen Lite | 7' - 0" | 37055 | 4 | 2 | 7' - 2" | 3' - 2" | 2' - 10" |
| 37055 Thermal French 34x96 Ovolo Flat Panel | Thermal French TDL - Fifteen Lite | 8' - 0" | 37055 | 4 | 2 | 8' - 2" | 3' - 2" | 2' - 10" |
| 37055 Thermal French 36x80 Ovolo Flat Panel | Thermal French TDL - Fifteen Lite | 6' - 8" | 37055 | 4 | 2 | 6' - 10" | 3' - 4" | 3' - 0" |
| 37055 Thermal French 36x84 Ovolo Flat Panel | Thermal French TDL - Fifteen Lite | 7' - 0" | 37055 | 4 | 2 | 7' - 2" | 3' - 4" | 3' - 0" |
| 37055 Thermal French 36x96 Ovolo Flat Panel | Thermal French TDL - Fifteen Lite | 8' - 0" | 37055 | 4 | 2 | 8' - 2" | 3' - 4" | 3' - 0" |
| 37055 Thermal French 38x80 Ovolo Flat Panel | Thermal French TDL - Fifteen Lite | 6' - 8" | 37055 | 4 | 2 | 6' - 10" | 3' - 6" | 3' - 2" |
| 37055 Thermal French 38x84 Ovolo Flat Panel | Thermal French TDL - Fifteen Lite | 7' - 0" | 37055 | 4 | 2 | 7' - 2" | 3' - 6" | 3' - 2" |
| 37055 Thermal French 38x96 Ovolo Flat Panel | Thermal French TDL - Fifteen Lite | 8' - 0" | 37055 | 4 | 2 | 8' - 2" | 3' - 6" | 3' - 2" |
| 37055 Thermal French 40x80 Ovolo Flat Panel | Thermal French TDL - Fifteen Lite | 6' - 8" | 37055 | 4 | 2 | 6' - 10" | 3' - 8" | 3' - 4" |
| 37055 Thermal French 40x84 Ovolo Flat Panel | Thermal French TDL - Fifteen Lite | 7' - 0" | 37055 | 4 | 2 | 7' - 2" | 3' - 8" | 3' - 4" |
| 37055 Thermal French 40x96 Ovolo Flat Panel | Thermal French TDL - Fifteen Lite | 8' - 0" | 37055 | 4 | 2 | 8' - 2" | 3' - 8" | 3' - 4" |
| 37055 Thermal French 42x80 Ovolo Flat Panel | Thermal French TDL - Fifteen Lite | 6' - 8" | 37055 | 4 | 2 | 6' - 10" | 3' - 10" | 3' - 6" |
| 37055 Thermal French 42x84 Ovolo Flat Panel | Thermal French TDL - Fifteen Lite | 7' - 0" | 37055 | 4 | 2 | 7' - 2" | 3' - 10" | 3' - 6" |
| 37055 Thermal French 42x96 Ovolo Flat Panel | Thermal French TDL - Fifteen Lite | 8' - 0" | 37055 | 4 | 2 | 8' - 2" | 3' - 10" | 3' - 6" |
| 37056 Thermal French 30x80 Ovolo Flat Panel | Thermal French TDL - Six Lite | 6' - 8" | 37056 | 2 | 1 | 6' - 10" | 2' - 10" | 2' - 6" |
| 37056 Thermal French 30x84 Ovolo Flat Panel | Thermal French TDL - Six Lite | 7' - 0" | 37056 | 2 | 1 | 7' - 2" | 2' - 10" | 2' - 6" |
| 37056 Thermal French 30x96 Ovolo Flat Panel | Thermal French TDL - Six Lite | 8' - 0" | 37056 | 2 | 1 | 8' - 2" | 2' - 10" | 2' - 6" |
| 37056 Thermal French 32x80 Ovolo Flat Panel | Thermal French TDL - Six Lite | 6' - 8" | 37056 | 2 | 1 | 6' - 10" | 3' - 0" | 2' - 8" |
| 37056 Thermal French 32x84 Ovolo Flat Panel | Thermal French TDL - Six Lite | 7' - 0" | 37056 | 2 | 1 | 7' - 2" | 3' - 0" | 2' - 8" |
| 37056 Thermal French 32x96 Ovolo Flat Panel | Thermal French TDL - Six Lite | 8' - 0" | 37056 | 2 | 1 | 8' - 2" | 3' - 0" | 2' - 8" |
| 37056 Thermal French 34x80 Ovolo Flat Panel | Thermal French TDL - Six Lite | 6' - 8" | 37056 | 2 | 1 | 6' - 10" | 3' - 2" | 2' - 10" |
| 37056 Thermal French 34x84 Ovolo Flat Panel | Thermal French TDL - Six Lite | 7' - 0" | 37056 | 2 | 1 | 7' - 2" | 3' - 2" | 2' - 10" |
| 37056 Thermal French 34x96 Ovolo Flat Panel | Thermal French TDL - Six Lite | 8' - 0" | 37056 | 2 | 1 | 8' - 2" | 3' - 2" | 2' - 10" |
| 37056 Thermal French 36x80 Ovolo Flat Panel | Thermal French TDL - Six Lite | 6' - 8" | 37056 | 2 | 1 | 6' - 10" | 3' - 4" | 3' - 0" |
| 37056 Thermal French 36x84 Ovolo Flat Panel | Thermal French TDL - Six Lite | 7' - 0" | 37056 | 2 | 1 | 7' - 2" | 3' - 4" | 3' - 0" |
| 37056 Thermal French 36x96 Ovolo Flat Panel | Thermal French TDL - Six Lite | 8' - 0" | 37056 | 2 | 1 | 8' - 2" | 3' - 4" | 3' - 0" |
| 37056 Thermal French 38x80 Ovolo Flat Panel | Thermal French TDL - Six Lite | 6' - 8" | 37056 | 2 | 1 | 6' - 10" | 3' - 6" | 3' - 2" |
| 37056 Thermal French 38x84 Ovolo Flat Panel | Thermal French TDL - Six Lite | 7' - 0" | 37056 | 2 | 1 | 7' - 2" | 3' - 6" | 3' - 2" |
| 37056 Thermal French 38x96 Ovolo Flat Panel | Thermal French TDL - Six Lite | 8' - 0" | 37056 | 2 | 1 | 8' - 2" | 3' - 6" | 3' - 2" |
| 37056 Thermal French 40x80 Ovolo Flat Panel | Thermal French TDL - Six Lite | 6' - 8" | 37056 | 2 | 1 | 6' - 10" | 3' - 8" | 3' - 4" |
| 37056 Thermal French 40x84 Ovolo Flat Panel | Thermal French TDL - Six Lite | 7' - 0" | 37056 | 2 | 1 | 7' - 2" | 3' - 8" | 3' - 4" |
| 37056 Thermal French 40x96 Ovolo Flat Panel | Thermal French TDL - Six Lite | 8' - 0" | 37056 | 2 | 1 | 8' - 2" | 3' - 8" | 3' - 4" |
| 37056 Thermal French 42x80 Ovolo Flat Panel | Thermal French TDL - Six Lite | 6' - 8" | 37056 | 2 | 1 | 6' - 10" | 3' - 10" | 3' - 6" |
| 37056 Thermal French 42x84 Ovolo Flat Panel | Thermal French TDL - Six Lite | 7' - 0" | 37056 | 2 | 1 | 7' - 2" | 3' - 10" | 3' - 6" |
| 37056 Thermal French 42x96 Ovolo Flat Panel | Thermal French TDL - Six Lite | 8' - 0" | 37056 | 2 | 1 | 8' - 2" | 3' - 10" | 3' - 6" |
| 37058 Thermal French 30x80 Ovolo Flat Panel | Thermal French TDL - Eight Lite | 6' - 8" | 37058 | 3 | 1 | 6' - 10" | 2' - 10" | 2' - 6" |
| 37058 Thermal French 30x84 Ovolo Flat Panel | Thermal French TDL - Eight Lite | 7' - 0" | 37058 | 3 | 1 | 7' - 2" | 2' - 10" | 2' - 6" |
| 37058 Thermal French 30x96 Ovolo Flat Panel | Thermal French TDL - Eight Lite | 8' - 0" | 37058 | 3 | 1 | 8' - 2" | 2' - 10" | 2' - 6" |
| 37058 Thermal French 32x80 Ovolo Flat Panel | Thermal French TDL - Eight Lite | 6' - 8" | 37058 | 3 | 1 | 6' - 10" | 3' - 0" | 2' - 8" |
| 37058 Thermal French 32x84 Ovolo Flat Panel | Thermal French TDL - Eight Lite | 7' - 0" | 37058 | 3 | 1 | 7' - 2" | 3' - 0" | 2' - 8" |
| 37058 Thermal French 32x96 Ovolo Flat Panel | Thermal French TDL - Eight Lite | 8' - 0" | 37058 | 3 | 1 | 8' - 2" | 3' - 0" | 2' - 8" |
| 37058 Thermal French 34x80 Ovolo Flat Panel | Thermal French TDL - Eight Lite | 6' - 8" | 37058 | 3 | 1 | 6' - 10" | 3' - 2" | 2' - 10" |
| 37058 Thermal French 34x84 Ovolo Flat Panel | Thermal French TDL - Eight Lite | 7' - 0" | 37058 | 3 | 1 | 7' - 2" | 3' - 2" | 2' - 10" |
| 37058 Thermal French 34x96 Ovolo Flat Panel | Thermal French TDL - Eight Lite | 8' - 0" | 37058 | 3 | 1 | 8' - 2" | 3' - 2" | 2' - 10" |
| 37058 Thermal French 36x80 Ovolo Flat Panel | Thermal French TDL - Eight Lite | 6' - 8" | 37058 | 3 | 1 | 6' - 10" | 3' - 4" | 3' - 0" |
| 37058 Thermal French 36x84 Ovolo Flat Panel | Thermal French TDL - Eight Lite | 7' - 0" | 37058 | 3 | 1 | 7' - 2" | 3' - 4" | 3' - 0" |
| 37058 Thermal French 36x96 Ovolo Flat Panel | Thermal French TDL - Eight Lite | 8' - 0" | 37058 | 3 | 1 | 8' - 2" | 3' - 4" | 3' - 0" |
| 37058 Thermal French 38x80 Ovolo Flat Panel | Thermal French TDL - Eight Lite | 6' - 8" | 37058 | 3 | 1 | 6' - 10" | 3' - 6" | 3' - 2" |
| 37058 Thermal French 38x84 Ovolo Flat Panel | Thermal French TDL - Eight Lite | 7' - 0" | 37058 | 3 | 1 | 7' - 2" | 3' - 6" | 3' - 2" |
| 37058 Thermal French 38x96 Ovolo Flat Panel | Thermal French TDL - Eight Lite | 8' - 0" | 37058 | 3 | 1 | 8' - 2" | 3' - 6" | 3' - 2" |
| 37058 Thermal French 40x80 Ovolo Flat Panel | Thermal French TDL - Eight Lite | 6' - 8" | 37058 | 3 | 1 | 6' - 10" | 3' - 8" | 3' - 4" |
| 37058 Thermal French 40x84 Ovolo Flat Panel | Thermal French TDL - Eight Lite | 7' - 0" | 37058 | 3 | 1 | 7' - 2" | 3' - 8" | 3' - 4" |
| 37058 Thermal French 40x96 Ovolo Flat Panel | Thermal French TDL - Eight Lite | 8' - 0" | 37058 | 3 | 1 | 8' - 2" | 3' - 8" | 3' - 4" |
| 37058 Thermal French 42x80 Ovolo Flat Panel | Thermal French TDL - Eight Lite | 6' - 8" | 37058 | 3 | 1 | 6' - 10" | 3' - 10" | 3' - 6" |
| 37058 Thermal French 42x84 Ovolo Flat Panel | Thermal French TDL - Eight Lite | 7' - 0" | 37058 | 3 | 1 | 7' - 2" | 3' - 10" | 3' - 6" |
| 37058 Thermal French 42x96 Ovolo Flat Panel | Thermal French TDL - Eight Lite | 8' - 0" | 37058 | 3 | 1 | 8' - 2" | 3' - 10" | 3' - 6" |

## geometry (parser evidence)
native form markers: Blend x30, Sweep x15
no freeform markers — native parametric forms only
